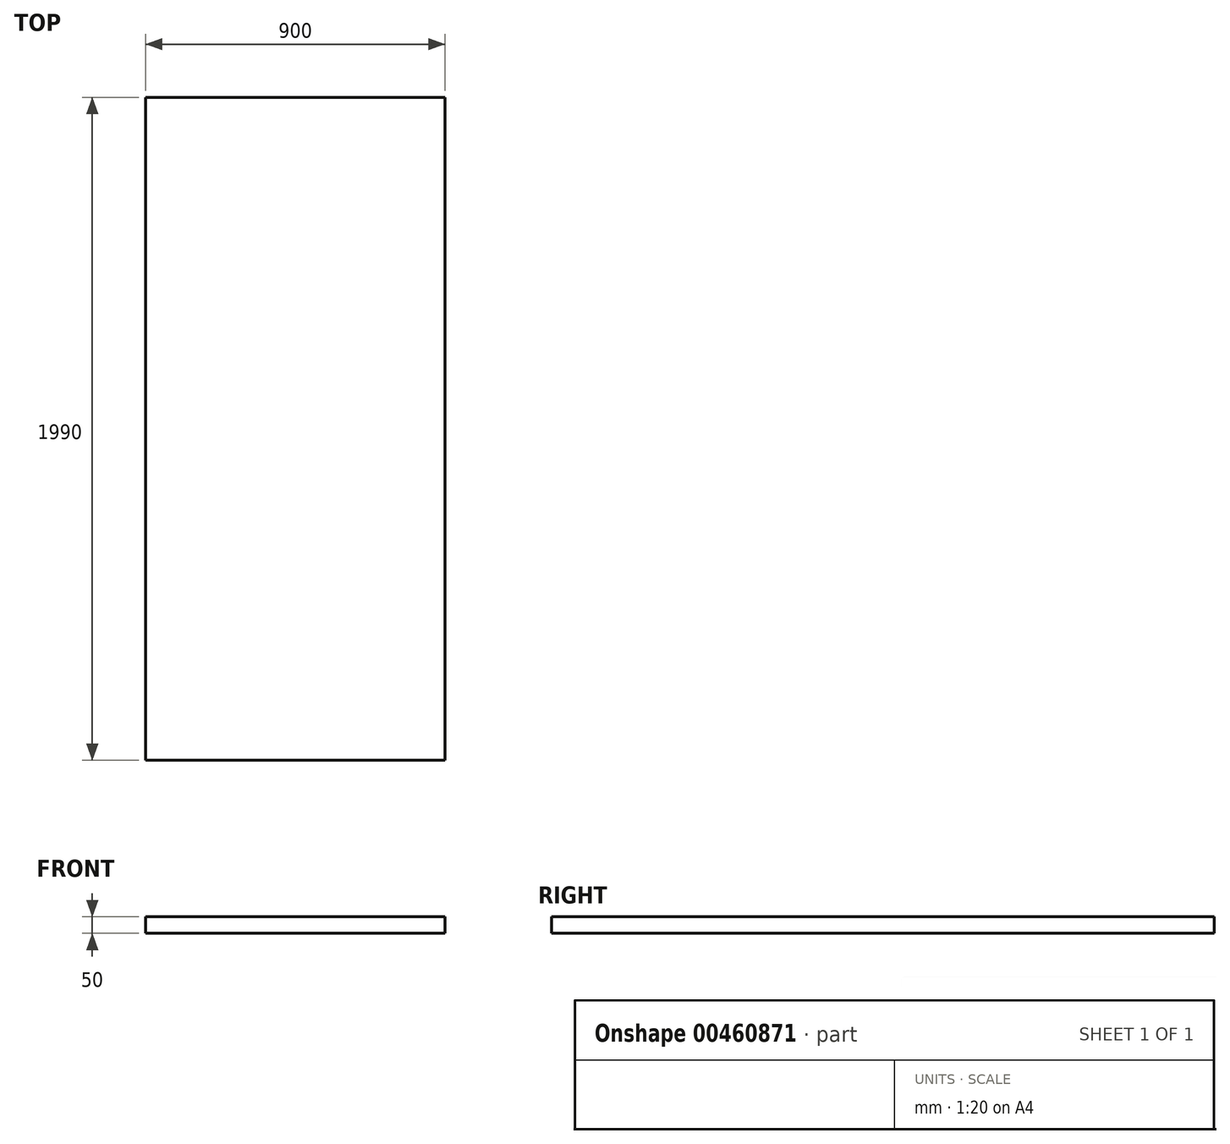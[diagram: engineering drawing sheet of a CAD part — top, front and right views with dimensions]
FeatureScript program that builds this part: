
annotation { "Feature Type Name" : "Feature", "Feature Type Description" : "" }
export const myFeature = defineFeature(function(context is Context, id is Id, definition is map)
    precondition{}
    {
        {
            var Q0;
            Q0=qCreatedBy(makeId("Top.planeOp"),FACE);
            var sketch = newSketch(context, id + "F0", { "sketchPlane" : qUnion([Q0])});
            skLineSegment(sketch, "E0.bottom", {"start": v(-525.8, 740.5) * mm, "end": v(374.2, 740.5) * mm});
            skLineSegment(sketch, "E0.top", {"start": v(-525.8, -1249.5) * mm, "end": v(374.2, -1249.5) * mm});
            skLineSegment(sketch, "E0.left", {"start": v(-525.8, 740.5) * mm, "end": v(-525.8, -1249.5) * mm});
            skLineSegment(sketch, "E0.right", {"start": v(374.2, 740.5) * mm, "end": v(374.2, -1249.5) * mm});
            skSolve(sketch);
        }
        {
            var Q0;
            Q0 = qSketchRegion(id + "F0", true);
            extrude(context, id + "F1", {"entities" : qUnion([Q0]), "depth" : 50 * mm});
        }
    });
